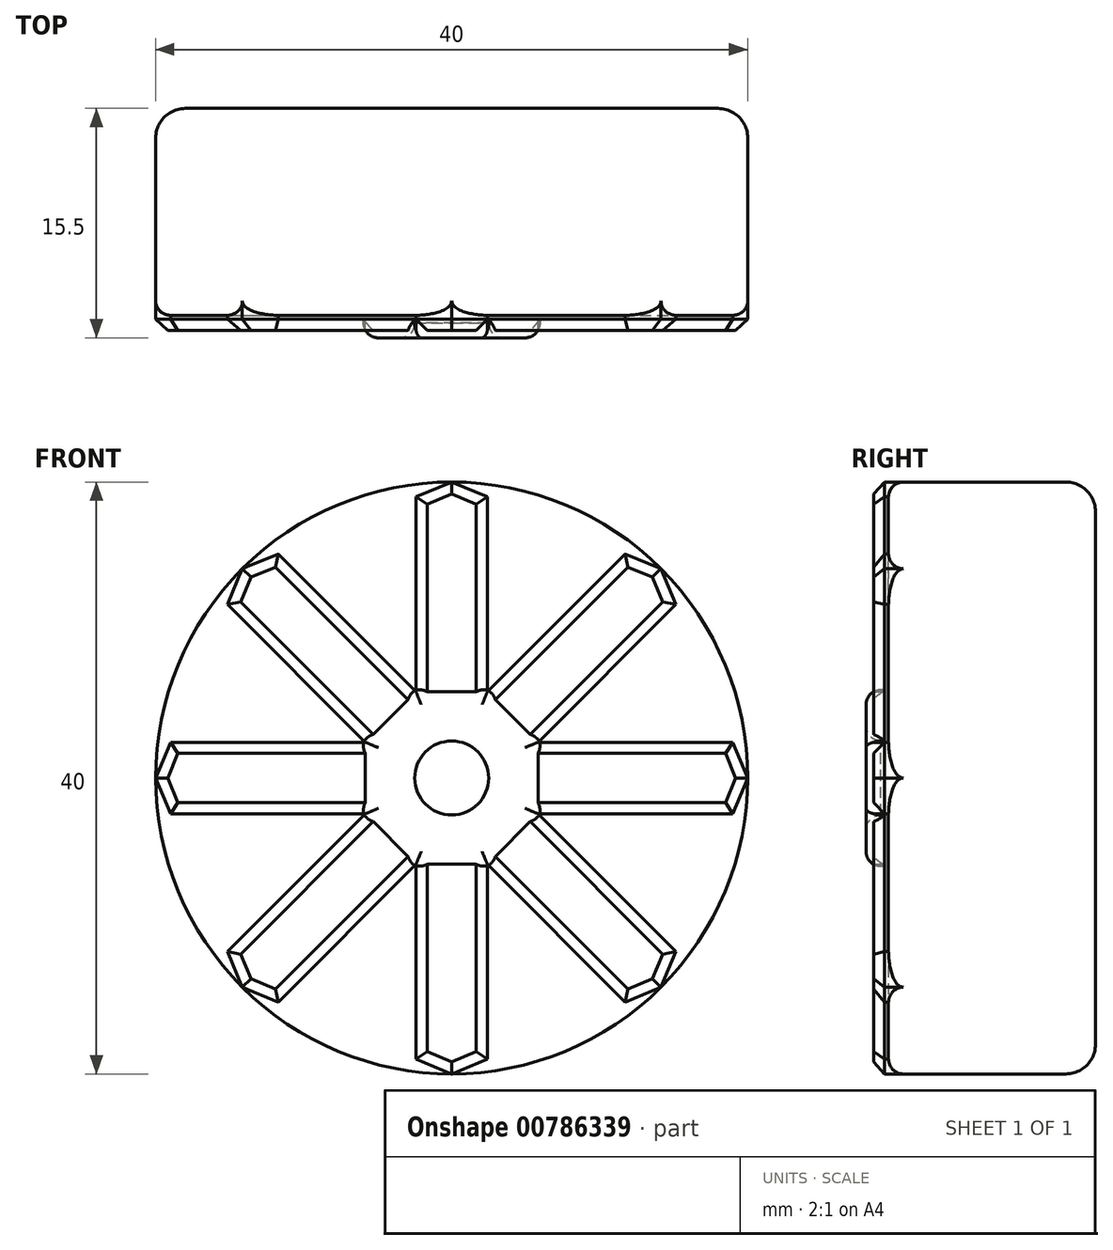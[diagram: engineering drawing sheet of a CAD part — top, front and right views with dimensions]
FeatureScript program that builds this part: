
annotation { "Feature Type Name" : "Feature", "Feature Type Description" : "" }
export const myFeature = defineFeature(function(context is Context, id is Id, definition is map)
    precondition{}
    {
        {
            var Q0;
            Q0=qCreatedBy(makeId("Front.planeOp"),FACE);
            var sketch = newSketch(context, id + "F0", { "sketchPlane" : qUnion([Q0])});
            skCircle(sketch, "E0", {"center": v(0, 0) * mm, "radius": 20 * mm});
            skSolve(sketch);
        }
        {
            var Q0;
            Q0 = qSketchRegion(id + "F0", true);
            extrude(context, id + "F1", {"entities" : qUnion([Q0]), "depth" : 14 * mm, "offsetDistance" : 25 * mm});
        }
        {
            var Q0;
            Q0=makeQuery(id+"F1.opExtrude","CAP_FACE",FACE,{"disambiguationData":[OSD([sQuery(id+"F0.wireOp",EDGE,"E0")])],"isStart":false});
            var sketch = newSketch(context, id + "F2", { "sketchPlane" : qUnion([Q0])});
            skCircle(sketch, "E1.cCircle", {"center": v(0, 0) * mm, "radius": 20 * mm, "construction": true});
            skLineSegment(sketch, "E1.1", {"start": v(14.14, 14.14) * mm, "end": v(15.14, 11.73) * mm});
            skLineSegment(sketch, "E1.2", {"start": v(20, 0) * mm, "end": v(19, -2.41) * mm});
            skLineSegment(sketch, "E1.3", {"start": v(14.14, -14.14) * mm, "end": v(11.73, -15.14) * mm});
            skLineSegment(sketch, "E1.4", {"start": v(0, -20) * mm, "end": v(-2.41, -19) * mm});
            skLineSegment(sketch, "E1.5", {"start": v(-14.14, -14.14) * mm, "end": v(-15.14, -11.73) * mm});
            skLineSegment(sketch, "E1.6", {"start": v(-20, 0) * mm, "end": v(-19, 2.41) * mm});
            skLineSegment(sketch, "E1.7", {"start": v(-14.14, 14.14) * mm, "end": v(-11.73, 15.14) * mm});
            skCircle(sketch, "E2.cCircle", {"center": v(0, 0) * mm, "radius": 5 * mm, "construction": true});
            skLineSegment(sketch, "E3.left", {"start": v(-2.41, 19) * mm, "end": v(-2.41, 5.83) * mm});
            skLineSegment(sketch, "E3.right", {"start": v(2.41, 19) * mm, "end": v(2.41, 5.83) * mm});
            skLineSegment(sketch, "E4.bottom", {"start": v(-19, 2.41) * mm, "end": v(-5.83, 2.41) * mm});
            skLineSegment(sketch, "E4.top", {"start": v(-19, -2.41) * mm, "end": v(-5.83, -2.41) * mm});
            skLineSegment(sketch, "E5", {"start": v(-15.14, 11.73) * mm, "end": v(-5.83, 2.41) * mm});
            skLineSegment(sketch, "E6", {"start": v(-11.73, 15.14) * mm, "end": v(-2.41, 5.83) * mm});
            skLineSegment(sketch, "E7", {"start": v(-15.14, -11.73) * mm, "end": v(-5.83, -2.41) * mm});
            skLineSegment(sketch, "E8", {"start": v(15.14, 11.73) * mm, "end": v(5.83, 2.41) * mm});
            skLineSegment(sketch, "E9.trimOffspring", {"start": v(-2.41, 19) * mm, "end": v(0, 20) * mm});
            skLineSegment(sketch, "E10.trimOffspring", {"start": v(-15.14, 11.73) * mm, "end": v(-14.14, 14.14) * mm});
            skLineSegment(sketch, "E11.trimOffspring", {"start": v(-19, -2.41) * mm, "end": v(-20, 0) * mm});
            skLineSegment(sketch, "E12.trimOffspring", {"start": v(-11.73, -15.14) * mm, "end": v(-14.14, -14.14) * mm});
            skLineSegment(sketch, "E13.trimOffspring", {"start": v(2.41, -19) * mm, "end": v(0, -20) * mm});
            skLineSegment(sketch, "E14.trimOffspring", {"start": v(15.14, -11.73) * mm, "end": v(14.14, -14.14) * mm});
            skLineSegment(sketch, "E15.trimOffspring", {"start": v(19, 2.41) * mm, "end": v(20, 0) * mm});
            skLineSegment(sketch, "E16.trimOffspring", {"start": v(11.73, 15.14) * mm, "end": v(14.14, 14.14) * mm});
            skLineSegment(sketch, "E17.trimOffspring", {"start": v(2.41, -5.83) * mm, "end": v(11.73, -15.14) * mm});
            skPoint(sketch, "E18.orphan", {"position": v(-5, 0) * mm});
            skPoint(sketch, "E19.orphan", {"position": v(-3.54, 3.54) * mm});
            skLineSegment(sketch, "E20.trimOffspring", {"start": v(5.83, -2.41) * mm, "end": v(15.14, -11.73) * mm});
            skPoint(sketch, "E21.orphan", {"position": v(0, 5) * mm});
            skLineSegment(sketch, "E22.trimOffspring", {"start": v(2.41, 5.83) * mm, "end": v(11.73, 15.14) * mm});
            skLineSegment(sketch, "E23.trimOffspring", {"start": v(2.41, -5.83) * mm, "end": v(2.41, -19) * mm});
            skLineSegment(sketch, "E24.trimOffspring", {"start": v(5.83, 2.41) * mm, "end": v(19, 2.41) * mm});
            skPoint(sketch, "E25.orphan", {"position": v(3.54, 3.54) * mm});
            skPoint(sketch, "E26.orphan", {"position": v(5, 0) * mm});
            skLineSegment(sketch, "E27.trimOffspring", {"start": v(5.83, -2.41) * mm, "end": v(19, -2.41) * mm});
            skLineSegment(sketch, "E28.trimOffspring", {"start": v(-2.41, -5.83) * mm, "end": v(-2.41, -19) * mm});
            skLineSegment(sketch, "E29.trimOffspring", {"start": v(-2.41, -5.83) * mm, "end": v(-11.73, -15.14) * mm});
            skLineSegment(sketch, "E30", {"start": v(2.41, 19) * mm, "end": v(0, 20) * mm});
            skSolve(sketch);
        }
        {
            var Q0;
            Q0 = qSketchRegion(id + "F2", true);
            extrude(context, id + "F3", {"entities" : qUnion([Q0]), "operationType" : NewBodyOperationType.ADD, "depth" : 1 * mm, "offsetDistance" : 25 * mm});
        }
        {
            var Q0;
            Q0=makeQuery(id+"F3.opExtrude","CAP_FACE",FACE,{"disambiguationData":[OSD([sQuery(id+"F2.wireOp",EDGE,"E1.1"),sQuery(id+"F2.wireOp",EDGE,"E1.2"),sQuery(id+"F2.wireOp",EDGE,"E1.3"),sQuery(id+"F2.wireOp",EDGE,"E1.4"),sQuery(id+"F2.wireOp",EDGE,"E1.5"),sQuery(id+"F2.wireOp",EDGE,"E1.6"),sQuery(id+"F2.wireOp",EDGE,"E1.7"),sQuery(id+"F2.wireOp",EDGE,"E3.left"),sQuery(id+"F2.wireOp",EDGE,"E3.right"),sQuery(id+"F2.wireOp",EDGE,"E4.bottom"),sQuery(id+"F2.wireOp",EDGE,"E4.top"),sQuery(id+"F2.wireOp",EDGE,"E5"),sQuery(id+"F2.wireOp",EDGE,"E6"),sQuery(id+"F2.wireOp",EDGE,"E7"),sQuery(id+"F2.wireOp",EDGE,"E8"),sQuery(id+"F2.wireOp",EDGE,"E9.trimOffspring"),sQuery(id+"F2.wireOp",EDGE,"E10.trimOffspring"),sQuery(id+"F2.wireOp",EDGE,"E11.trimOffspring"),sQuery(id+"F2.wireOp",EDGE,"E12.trimOffspring"),sQuery(id+"F2.wireOp",EDGE,"E13.trimOffspring"),sQuery(id+"F2.wireOp",EDGE,"E14.trimOffspring"),sQuery(id+"F2.wireOp",EDGE,"E15.trimOffspring"),sQuery(id+"F2.wireOp",EDGE,"E16.trimOffspring"),sQuery(id+"F2.wireOp",EDGE,"E17.trimOffspring"),sQuery(id+"F2.wireOp",EDGE,"E20.trimOffspring"),sQuery(id+"F2.wireOp",EDGE,"E22.trimOffspring"),sQuery(id+"F2.wireOp",EDGE,"E23.trimOffspring"),sQuery(id+"F2.wireOp",EDGE,"E24.trimOffspring"),sQuery(id+"F2.wireOp",EDGE,"E27.trimOffspring"),sQuery(id+"F2.wireOp",EDGE,"E28.trimOffspring"),sQuery(id+"F2.wireOp",EDGE,"E29.trimOffspring"),sQuery(id+"F2.wireOp",EDGE,"E30")])],"isStart":false});
            var sketch = newSketch(context, id + "F4", { "sketchPlane" : qUnion([Q0])});
            skCircle(sketch, "E31.cCircle", {"center": v(0, 0) * mm, "radius": 6.3 * mm, "construction": true});
            skLineSegment(sketch, "E31.0", {"start": v(-2.41, 5.83) * mm, "end": v(2.41, 5.83) * mm});
            skLineSegment(sketch, "E31.1", {"start": v(2.41, 5.83) * mm, "end": v(5.83, 2.41) * mm});
            skLineSegment(sketch, "E31.2", {"start": v(5.83, 2.41) * mm, "end": v(5.83, -2.41) * mm});
            skLineSegment(sketch, "E31.3", {"start": v(5.83, -2.41) * mm, "end": v(2.41, -5.83) * mm});
            skLineSegment(sketch, "E31.4", {"start": v(2.41, -5.83) * mm, "end": v(-2.41, -5.83) * mm});
            skLineSegment(sketch, "E31.5", {"start": v(-2.41, -5.83) * mm, "end": v(-5.83, -2.41) * mm});
            skLineSegment(sketch, "E31.6", {"start": v(-5.83, -2.41) * mm, "end": v(-5.83, 2.41) * mm});
            skLineSegment(sketch, "E31.7", {"start": v(-5.83, 2.41) * mm, "end": v(-2.41, 5.83) * mm});
            skSolve(sketch);
        }
        {
            var Q0;
            Q0 = qSketchRegion(id + "F4", true);
            extrude(context, id + "F5", {"entities" : qUnion([Q0]), "operationType" : NewBodyOperationType.ADD, "depth" : 0.5 * mm, "offsetDistance" : 25 * mm});
        }
        {
            var Q0;
            Q0=makeQuery(id+"F5.opExtrude","CAP_FACE",FACE,{"disambiguationData":[OSD([sQuery(id+"F4.wireOp",EDGE,"E31.0"),sQuery(id+"F4.wireOp",EDGE,"E31.1"),sQuery(id+"F4.wireOp",EDGE,"E31.2"),sQuery(id+"F4.wireOp",EDGE,"E31.3"),sQuery(id+"F4.wireOp",EDGE,"E31.4"),sQuery(id+"F4.wireOp",EDGE,"E31.5"),sQuery(id+"F4.wireOp",EDGE,"E31.6"),sQuery(id+"F4.wireOp",EDGE,"E31.7")])],"isStart":false});
            var sketch = newSketch(context, id + "F6", { "sketchPlane" : qUnion([Q0])});
            skCircle(sketch, "E32", {"center": v(0, 0) * mm, "radius": 2.5 * mm});
            skSolve(sketch);
        }
        {
            var Q0;
            Q0 = qSketchRegion(id + "F6", true);
            extrude(context, id + "F7", {"entities" : qUnion([Q0]), "operationType" : NewBodyOperationType.REMOVE, "oppositeDirection" : true, "depth" : 1 * mm, "offsetDistance" : 25 * mm});
        }
        {
            var Q0;
            {var subQ0=sQuery(id+"F0.wireOp",EDGE,"E0");Q0=makeQuery(id+"F3.boolean.opBoolean","SPLIT",EDGE,{"disambiguationData":[TD([makeQuery(id+"F1.opExtrude","SWEPT_FACE",FACE,{"disambiguationData":[OSD([subQ0])]}),makeQuery(id+"F1.opExtrude","CAP_FACE",FACE,{"disambiguationData":[OSD([subQ0])],"isStart":false}),makeQuery(id+"F3.opExtrude","SWEPT_FACE",FACE,{"disambiguationData":[OSD([sQuery(id+"F2.wireOp",EDGE,"E1.6")])]}),makeQuery(id+"F3.opExtrude","SWEPT_FACE",FACE,{"disambiguationData":[OSD([sQuery(id+"F2.wireOp",EDGE,"E1.7")])]}),makeQuery(id+"F3.opExtrude","SWEPT_FACE",FACE,{"disambiguationData":[OSD([sQuery(id+"F2.wireOp",EDGE,"E10.trimOffspring")])]}),makeQuery(id+"F3.opExtrude","SWEPT_FACE",FACE,{"disambiguationData":[OSD([sQuery(id+"F2.wireOp",EDGE,"E11.trimOffspring")])]})])],"derivedFrom":makeQuery(id+"F1.opExtrude","CAP_EDGE",EDGE,{"disambiguationData":[OSD([subQ0])],"isStart":false})});}
            var Q1;
            {var subQ0=sQuery(id+"F0.wireOp",EDGE,"E0");Q1=makeQuery(id+"F3.boolean.opBoolean","SPLIT",EDGE,{"disambiguationData":[TD([makeQuery(id+"F1.opExtrude","SWEPT_FACE",FACE,{"disambiguationData":[OSD([subQ0])]}),makeQuery(id+"F1.opExtrude","CAP_FACE",FACE,{"disambiguationData":[OSD([subQ0])],"isStart":false}),makeQuery(id+"F3.opExtrude","SWEPT_FACE",FACE,{"disambiguationData":[OSD([sQuery(id+"F2.wireOp",EDGE,"E1.5")])]}),makeQuery(id+"F3.opExtrude","SWEPT_FACE",FACE,{"disambiguationData":[OSD([sQuery(id+"F2.wireOp",EDGE,"E1.6")])]}),makeQuery(id+"F3.opExtrude","SWEPT_FACE",FACE,{"disambiguationData":[OSD([sQuery(id+"F2.wireOp",EDGE,"E11.trimOffspring")])]}),makeQuery(id+"F3.opExtrude","SWEPT_FACE",FACE,{"disambiguationData":[OSD([sQuery(id+"F2.wireOp",EDGE,"E12.trimOffspring")])]})])],"derivedFrom":makeQuery(id+"F1.opExtrude","CAP_EDGE",EDGE,{"disambiguationData":[OSD([subQ0])],"isStart":false})});}
            var Q2;
            {var subQ0=sQuery(id+"F0.wireOp",EDGE,"E0");Q2=makeQuery(id+"F3.boolean.opBoolean","SPLIT",EDGE,{"disambiguationData":[TD([makeQuery(id+"F1.opExtrude","SWEPT_FACE",FACE,{"disambiguationData":[OSD([subQ0])]}),makeQuery(id+"F1.opExtrude","CAP_FACE",FACE,{"disambiguationData":[OSD([subQ0])],"isStart":false}),makeQuery(id+"F3.opExtrude","SWEPT_FACE",FACE,{"disambiguationData":[OSD([sQuery(id+"F2.wireOp",EDGE,"E1.7")])]}),makeQuery(id+"F3.opExtrude","SWEPT_FACE",FACE,{"disambiguationData":[OSD([sQuery(id+"F2.wireOp",EDGE,"E9.trimOffspring")])]}),makeQuery(id+"F3.opExtrude","SWEPT_FACE",FACE,{"disambiguationData":[OSD([sQuery(id+"F2.wireOp",EDGE,"E10.trimOffspring")])]}),makeQuery(id+"F3.opExtrude","SWEPT_FACE",FACE,{"disambiguationData":[OSD([sQuery(id+"F2.wireOp",EDGE,"E30")])]})])],"derivedFrom":makeQuery(id+"F1.opExtrude","CAP_EDGE",EDGE,{"disambiguationData":[OSD([subQ0])],"isStart":false})});}
            var Q3;
            {var subQ0=sQuery(id+"F0.wireOp",EDGE,"E0");Q3=makeQuery(id+"F3.boolean.opBoolean","SPLIT",EDGE,{"disambiguationData":[TD([makeQuery(id+"F1.opExtrude","SWEPT_FACE",FACE,{"disambiguationData":[OSD([subQ0])]}),makeQuery(id+"F1.opExtrude","CAP_FACE",FACE,{"disambiguationData":[OSD([subQ0])],"isStart":false}),makeQuery(id+"F3.opExtrude","SWEPT_FACE",FACE,{"disambiguationData":[OSD([sQuery(id+"F2.wireOp",EDGE,"E1.1")])]}),makeQuery(id+"F3.opExtrude","SWEPT_FACE",FACE,{"disambiguationData":[OSD([sQuery(id+"F2.wireOp",EDGE,"E9.trimOffspring")])]}),makeQuery(id+"F3.opExtrude","SWEPT_FACE",FACE,{"disambiguationData":[OSD([sQuery(id+"F2.wireOp",EDGE,"E16.trimOffspring")])]}),makeQuery(id+"F3.opExtrude","SWEPT_FACE",FACE,{"disambiguationData":[OSD([sQuery(id+"F2.wireOp",EDGE,"E30")])]})])],"derivedFrom":makeQuery(id+"F1.opExtrude","CAP_EDGE",EDGE,{"disambiguationData":[OSD([subQ0])],"isStart":false})});}
            var Q4;
            {var subQ0=sQuery(id+"F0.wireOp",EDGE,"E0");Q4=makeQuery(id+"F3.boolean.opBoolean","SPLIT",EDGE,{"disambiguationData":[TD([makeQuery(id+"F1.opExtrude","SWEPT_FACE",FACE,{"disambiguationData":[OSD([subQ0])]}),makeQuery(id+"F1.opExtrude","CAP_FACE",FACE,{"disambiguationData":[OSD([subQ0])],"isStart":false}),makeQuery(id+"F3.opExtrude","SWEPT_FACE",FACE,{"disambiguationData":[OSD([sQuery(id+"F2.wireOp",EDGE,"E1.1")])]}),makeQuery(id+"F3.opExtrude","SWEPT_FACE",FACE,{"disambiguationData":[OSD([sQuery(id+"F2.wireOp",EDGE,"E1.2")])]}),makeQuery(id+"F3.opExtrude","SWEPT_FACE",FACE,{"disambiguationData":[OSD([sQuery(id+"F2.wireOp",EDGE,"E15.trimOffspring")])]}),makeQuery(id+"F3.opExtrude","SWEPT_FACE",FACE,{"disambiguationData":[OSD([sQuery(id+"F2.wireOp",EDGE,"E16.trimOffspring")])]})])],"derivedFrom":makeQuery(id+"F1.opExtrude","CAP_EDGE",EDGE,{"disambiguationData":[OSD([subQ0])],"isStart":false})});}
            var Q5;
            {var subQ0=sQuery(id+"F0.wireOp",EDGE,"E0");Q5=makeQuery(id+"F3.boolean.opBoolean","SPLIT",EDGE,{"disambiguationData":[TD([makeQuery(id+"F1.opExtrude","SWEPT_FACE",FACE,{"disambiguationData":[OSD([subQ0])]}),makeQuery(id+"F1.opExtrude","CAP_FACE",FACE,{"disambiguationData":[OSD([subQ0])],"isStart":false}),makeQuery(id+"F3.opExtrude","SWEPT_FACE",FACE,{"disambiguationData":[OSD([sQuery(id+"F2.wireOp",EDGE,"E1.2")])]}),makeQuery(id+"F3.opExtrude","SWEPT_FACE",FACE,{"disambiguationData":[OSD([sQuery(id+"F2.wireOp",EDGE,"E1.3")])]}),makeQuery(id+"F3.opExtrude","SWEPT_FACE",FACE,{"disambiguationData":[OSD([sQuery(id+"F2.wireOp",EDGE,"E14.trimOffspring")])]}),makeQuery(id+"F3.opExtrude","SWEPT_FACE",FACE,{"disambiguationData":[OSD([sQuery(id+"F2.wireOp",EDGE,"E15.trimOffspring")])]})])],"derivedFrom":makeQuery(id+"F1.opExtrude","CAP_EDGE",EDGE,{"disambiguationData":[OSD([subQ0])],"isStart":false})});}
            var Q6;
            {var subQ0=sQuery(id+"F0.wireOp",EDGE,"E0");Q6=makeQuery(id+"F3.boolean.opBoolean","SPLIT",EDGE,{"disambiguationData":[TD([makeQuery(id+"F1.opExtrude","SWEPT_FACE",FACE,{"disambiguationData":[OSD([subQ0])]}),makeQuery(id+"F1.opExtrude","CAP_FACE",FACE,{"disambiguationData":[OSD([subQ0])],"isStart":false}),makeQuery(id+"F3.opExtrude","SWEPT_FACE",FACE,{"disambiguationData":[OSD([sQuery(id+"F2.wireOp",EDGE,"E1.3")])]}),makeQuery(id+"F3.opExtrude","SWEPT_FACE",FACE,{"disambiguationData":[OSD([sQuery(id+"F2.wireOp",EDGE,"E1.4")])]}),makeQuery(id+"F3.opExtrude","SWEPT_FACE",FACE,{"disambiguationData":[OSD([sQuery(id+"F2.wireOp",EDGE,"E13.trimOffspring")])]}),makeQuery(id+"F3.opExtrude","SWEPT_FACE",FACE,{"disambiguationData":[OSD([sQuery(id+"F2.wireOp",EDGE,"E14.trimOffspring")])]})])],"derivedFrom":makeQuery(id+"F1.opExtrude","CAP_EDGE",EDGE,{"disambiguationData":[OSD([subQ0])],"isStart":false})});}
            var Q7;
            {var subQ0=sQuery(id+"F0.wireOp",EDGE,"E0");Q7=makeQuery(id+"F3.boolean.opBoolean","SPLIT",EDGE,{"disambiguationData":[TD([makeQuery(id+"F1.opExtrude","SWEPT_FACE",FACE,{"disambiguationData":[OSD([subQ0])]}),makeQuery(id+"F1.opExtrude","CAP_FACE",FACE,{"disambiguationData":[OSD([subQ0])],"isStart":false}),makeQuery(id+"F3.opExtrude","SWEPT_FACE",FACE,{"disambiguationData":[OSD([sQuery(id+"F2.wireOp",EDGE,"E1.4")])]}),makeQuery(id+"F3.opExtrude","SWEPT_FACE",FACE,{"disambiguationData":[OSD([sQuery(id+"F2.wireOp",EDGE,"E1.5")])]}),makeQuery(id+"F3.opExtrude","SWEPT_FACE",FACE,{"disambiguationData":[OSD([sQuery(id+"F2.wireOp",EDGE,"E12.trimOffspring")])]}),makeQuery(id+"F3.opExtrude","SWEPT_FACE",FACE,{"disambiguationData":[OSD([sQuery(id+"F2.wireOp",EDGE,"E13.trimOffspring")])]})])],"derivedFrom":makeQuery(id+"F1.opExtrude","CAP_EDGE",EDGE,{"disambiguationData":[OSD([subQ0])],"isStart":false})});}
            fillet(context, id + "F8", {"entities" : qUnion([Q0, Q1, Q2, Q3, Q4, Q5, Q6, Q7]), "radius" : 1 * mm, "tangentPropagation" : true, "allowEdgeOverflow" : false});
        }
        {
            var Q0;
            Q0=makeQuery(id+"F5.opExtrude","CAP_FACE",FACE,{"disambiguationData":[OSD([sQuery(id+"F4.wireOp",EDGE,"E31.0"),sQuery(id+"F4.wireOp",EDGE,"E31.1"),sQuery(id+"F4.wireOp",EDGE,"E31.2"),sQuery(id+"F4.wireOp",EDGE,"E31.3"),sQuery(id+"F4.wireOp",EDGE,"E31.4"),sQuery(id+"F4.wireOp",EDGE,"E31.5"),sQuery(id+"F4.wireOp",EDGE,"E31.6"),sQuery(id+"F4.wireOp",EDGE,"E31.7")])],"isStart":false});
            fillet(context, id + "F9", {"entities" : qUnion([Q0]), "radius" : 1 * mm, "tangentPropagation" : true, "allowEdgeOverflow" : false});
        }
        {
            var Q0;
            Q0=makeQuery(id+"F3.opExtrude","CAP_EDGE",EDGE,{"disambiguationData":[OSD([sQuery(id+"F2.wireOp",EDGE,"E3.left")])],"isStart":false});
            var Q1;
            Q1=makeQuery(id+"F3.opExtrude","CAP_EDGE",EDGE,{"disambiguationData":[OSD([sQuery(id+"F2.wireOp",EDGE,"E9.trimOffspring")])],"isStart":false});
            var Q2;
            Q2=makeQuery(id+"F3.opExtrude","CAP_EDGE",EDGE,{"disambiguationData":[OSD([sQuery(id+"F2.wireOp",EDGE,"E30")])],"isStart":false});
            var Q3;
            Q3=makeQuery(id+"F3.opExtrude","CAP_EDGE",EDGE,{"disambiguationData":[OSD([sQuery(id+"F2.wireOp",EDGE,"E3.right")])],"isStart":false});
            var Q4;
            Q4=makeQuery(id+"F3.opExtrude","CAP_EDGE",EDGE,{"disambiguationData":[OSD([sQuery(id+"F2.wireOp",EDGE,"E22.trimOffspring")])],"isStart":false});
            var Q5;
            Q5=makeQuery(id+"F3.opExtrude","CAP_EDGE",EDGE,{"disambiguationData":[OSD([sQuery(id+"F2.wireOp",EDGE,"E16.trimOffspring")])],"isStart":false});
            var Q6;
            Q6=makeQuery(id+"F3.opExtrude","CAP_EDGE",EDGE,{"disambiguationData":[OSD([sQuery(id+"F2.wireOp",EDGE,"E1.1")])],"isStart":false});
            var Q7;
            Q7=makeQuery(id+"F3.opExtrude","CAP_EDGE",EDGE,{"disambiguationData":[OSD([sQuery(id+"F2.wireOp",EDGE,"E8")])],"isStart":false});
            var Q8;
            Q8=makeQuery(id+"F3.opExtrude","CAP_EDGE",EDGE,{"disambiguationData":[OSD([sQuery(id+"F2.wireOp",EDGE,"E24.trimOffspring")])],"isStart":false});
            var Q9;
            Q9=makeQuery(id+"F3.opExtrude","CAP_EDGE",EDGE,{"disambiguationData":[OSD([sQuery(id+"F2.wireOp",EDGE,"E15.trimOffspring")])],"isStart":false});
            var Q10;
            Q10=makeQuery(id+"F3.opExtrude","CAP_EDGE",EDGE,{"disambiguationData":[OSD([sQuery(id+"F2.wireOp",EDGE,"E1.2")])],"isStart":false});
            var Q11;
            Q11=makeQuery(id+"F3.opExtrude","CAP_EDGE",EDGE,{"disambiguationData":[OSD([sQuery(id+"F2.wireOp",EDGE,"E27.trimOffspring")])],"isStart":false});
            var Q12;
            Q12=makeQuery(id+"F3.opExtrude","CAP_EDGE",EDGE,{"disambiguationData":[OSD([sQuery(id+"F2.wireOp",EDGE,"E20.trimOffspring")])],"isStart":false});
            var Q13;
            Q13=makeQuery(id+"F3.opExtrude","CAP_EDGE",EDGE,{"disambiguationData":[OSD([sQuery(id+"F2.wireOp",EDGE,"E14.trimOffspring")])],"isStart":false});
            var Q14;
            Q14=makeQuery(id+"F3.opExtrude","CAP_EDGE",EDGE,{"disambiguationData":[OSD([sQuery(id+"F2.wireOp",EDGE,"E1.3")])],"isStart":false});
            var Q15;
            Q15=makeQuery(id+"F3.opExtrude","CAP_EDGE",EDGE,{"disambiguationData":[OSD([sQuery(id+"F2.wireOp",EDGE,"E17.trimOffspring")])],"isStart":false});
            var Q16;
            Q16=makeQuery(id+"F3.opExtrude","CAP_EDGE",EDGE,{"disambiguationData":[OSD([sQuery(id+"F2.wireOp",EDGE,"E23.trimOffspring")])],"isStart":false});
            var Q17;
            Q17=makeQuery(id+"F3.opExtrude","CAP_EDGE",EDGE,{"disambiguationData":[OSD([sQuery(id+"F2.wireOp",EDGE,"E13.trimOffspring")])],"isStart":false});
            var Q18;
            Q18=makeQuery(id+"F3.opExtrude","CAP_EDGE",EDGE,{"disambiguationData":[OSD([sQuery(id+"F2.wireOp",EDGE,"E1.4")])],"isStart":false});
            var Q19;
            Q19=makeQuery(id+"F3.opExtrude","CAP_EDGE",EDGE,{"disambiguationData":[OSD([sQuery(id+"F2.wireOp",EDGE,"E28.trimOffspring")])],"isStart":false});
            var Q20;
            Q20=makeQuery(id+"F3.opExtrude","CAP_EDGE",EDGE,{"disambiguationData":[OSD([sQuery(id+"F2.wireOp",EDGE,"E29.trimOffspring")])],"isStart":false});
            var Q21;
            Q21=makeQuery(id+"F3.opExtrude","CAP_EDGE",EDGE,{"disambiguationData":[OSD([sQuery(id+"F2.wireOp",EDGE,"E12.trimOffspring")])],"isStart":false});
            var Q22;
            Q22=makeQuery(id+"F3.opExtrude","CAP_EDGE",EDGE,{"disambiguationData":[OSD([sQuery(id+"F2.wireOp",EDGE,"E1.5")])],"isStart":false});
            var Q23;
            Q23=makeQuery(id+"F3.opExtrude","CAP_EDGE",EDGE,{"disambiguationData":[OSD([sQuery(id+"F2.wireOp",EDGE,"E7")])],"isStart":false});
            var Q24;
            Q24=makeQuery(id+"F3.opExtrude","CAP_EDGE",EDGE,{"disambiguationData":[OSD([sQuery(id+"F2.wireOp",EDGE,"E4.top")])],"isStart":false});
            var Q25;
            Q25=makeQuery(id+"F3.opExtrude","CAP_EDGE",EDGE,{"disambiguationData":[OSD([sQuery(id+"F2.wireOp",EDGE,"E11.trimOffspring")])],"isStart":false});
            var Q26;
            Q26=makeQuery(id+"F3.opExtrude","CAP_EDGE",EDGE,{"disambiguationData":[OSD([sQuery(id+"F2.wireOp",EDGE,"E1.6")])],"isStart":false});
            var Q27;
            Q27=makeQuery(id+"F3.opExtrude","CAP_EDGE",EDGE,{"disambiguationData":[OSD([sQuery(id+"F2.wireOp",EDGE,"E4.bottom")])],"isStart":false});
            var Q28;
            Q28=makeQuery(id+"F3.opExtrude","CAP_EDGE",EDGE,{"disambiguationData":[OSD([sQuery(id+"F2.wireOp",EDGE,"E5")])],"isStart":false});
            var Q29;
            Q29=makeQuery(id+"F3.opExtrude","CAP_EDGE",EDGE,{"disambiguationData":[OSD([sQuery(id+"F2.wireOp",EDGE,"E6")])],"isStart":false});
            var Q30;
            Q30=makeQuery(id+"F3.opExtrude","CAP_EDGE",EDGE,{"disambiguationData":[OSD([sQuery(id+"F2.wireOp",EDGE,"E10.trimOffspring")])],"isStart":false});
            var Q31;
            Q31=makeQuery(id+"F3.opExtrude","CAP_EDGE",EDGE,{"disambiguationData":[OSD([sQuery(id+"F2.wireOp",EDGE,"E1.7")])],"isStart":false});
            chamfer(context, id + "F10", {"entities" : qUnion([Q0, Q1, Q2, Q3, Q4, Q5, Q6, Q7, Q8, Q9, Q10, Q11, Q12, Q13, Q14, Q15, Q16, Q17, Q18, Q19, Q20, Q21, Q22, Q23, Q24, Q25, Q26, Q27, Q28, Q29, Q30, Q31]), "width" : 0.75 * mm, "tangentPropagation" : true});
        }
        {
            var Q0;
            Q0=makeQuery(id+"F1.opExtrude","CAP_FACE",FACE,{"disambiguationData":[OSD([sQuery(id+"F0.wireOp",EDGE,"E0")])],"isStart":true});
            fillet(context, id + "F11", {"entities" : qUnion([Q0]), "radius" : 2 * mm, "tangentPropagation" : true, "allowEdgeOverflow" : false});
        }
    });
